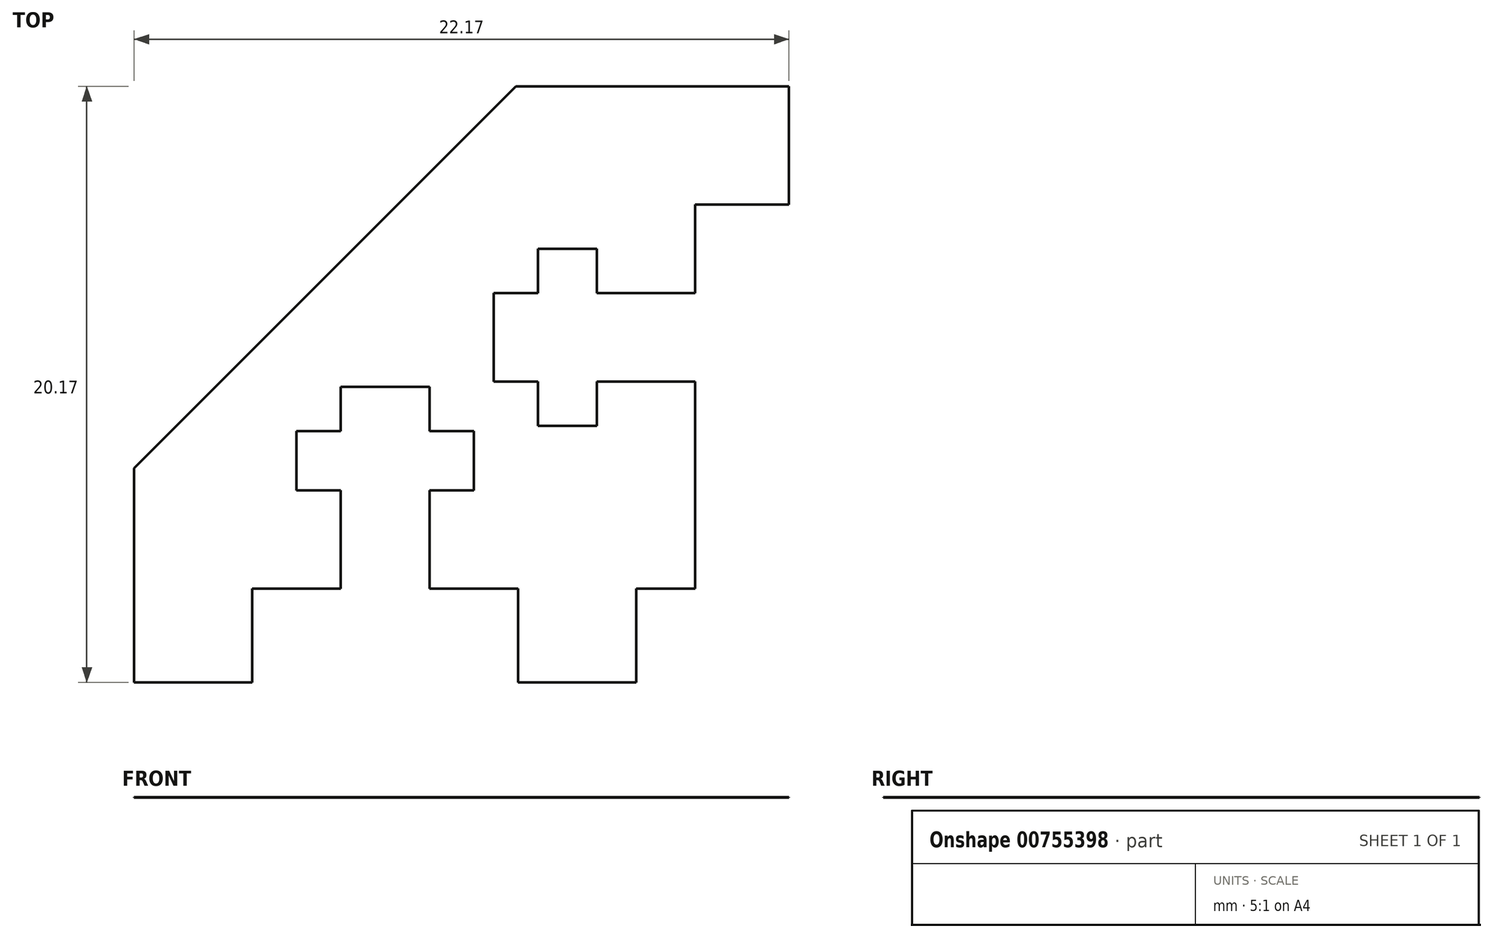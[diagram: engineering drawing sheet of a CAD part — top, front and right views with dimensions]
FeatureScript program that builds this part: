
annotation { "Feature Type Name" : "Feature", "Feature Type Description" : "" }
export const myFeature = defineFeature(function(context is Context, id is Id, definition is map)
    precondition{}
    {
        {
            var Q0;
            Q0=qCreatedBy(makeId("Top.planeOp"),FACE);
            var sketch = newSketch(context, id + "F0", { "sketchPlane" : qUnion([Q0])});
            skLineSegment(sketch, "E0.bottom", {"start": v(-25.65, 8.19) * mm, "end": v(-22.65, 8.19) * mm});
            skLineSegment(sketch, "E0.top", {"start": v(-25.65, -1.81) * mm, "end": v(-22.65, -1.81) * mm});
            skLineSegment(sketch, "E0.left", {"start": v(-25.65, 8.19) * mm, "end": v(-25.65, -1.81) * mm});
            skLineSegment(sketch, "E0.right", {"start": v(-22.65, 8.19) * mm, "end": v(-22.65, -1.81) * mm});
            skPoint(sketch, "E0.middle", {"position": v(-24.15, 3.19) * mm});
            skLineSegment(sketch, "E1.bottom", {"start": v(-27.15, 4.69) * mm, "end": v(-21.15, 4.69) * mm});
            skLineSegment(sketch, "E1.top", {"start": v(-27.15, 6.69) * mm, "end": v(-21.15, 6.69) * mm});
            skLineSegment(sketch, "E1.left", {"start": v(-27.15, 4.69) * mm, "end": v(-27.15, 6.69) * mm});
            skLineSegment(sketch, "E1.right", {"start": v(-21.15, 4.69) * mm, "end": v(-21.15, 6.69) * mm});
            skPoint(sketch, "E1.middle", {"position": v(-24.15, 5.69) * mm});
            skLineSegment(sketch, "E2", {"start": v(-24.15, 5.69) * mm, "end": v(-24.15, 3.19) * mm});
            skLineSegment(sketch, "E3.bottom", {"start": v(-28.65, -1.81) * mm, "end": v(-32.65, -1.81) * mm});
            skLineSegment(sketch, "E3.top", {"start": v(-28.65, 1.36) * mm, "end": v(-32.65, 1.36) * mm});
            skLineSegment(sketch, "E3.left", {"start": v(-28.65, -1.81) * mm, "end": v(-28.65, 1.36) * mm});
            skLineSegment(sketch, "E3.right", {"start": v(-32.65, -1.81) * mm, "end": v(-32.65, 1.36) * mm});
            skLineSegment(sketch, "E4.MirrorCS", {"start": v(-19.65, 1.36) * mm, "end": v(-15.65, 1.36) * mm});
            skLineSegment(sketch, "E5.MirrorCS", {"start": v(-19.65, -1.81) * mm, "end": v(-19.65, 1.36) * mm});
            skLineSegment(sketch, "E6.MirrorCS", {"start": v(-15.65, -1.81) * mm, "end": v(-15.65, 1.36) * mm});
            skLineSegment(sketch, "E7.MirrorCS", {"start": v(-19.65, -1.81) * mm, "end": v(-15.65, -1.81) * mm});
            skLineSegment(sketch, "E8", {"start": v(-19.65, 1.36) * mm, "end": v(-28.65, 1.36) * mm});
            skLineSegment(sketch, "E9.bottom", {"start": v(-28.65, 1.36) * mm, "end": v(-15.65, 1.36) * mm});
            skLineSegment(sketch, "E10.bottom", {"start": v(-20.48, 11.36) * mm, "end": v(-10.48, 11.36) * mm});
            skLineSegment(sketch, "E10.top", {"start": v(-20.48, 8.36) * mm, "end": v(-10.48, 8.36) * mm});
            skLineSegment(sketch, "E10.left", {"start": v(-20.48, 11.36) * mm, "end": v(-20.48, 8.36) * mm});
            skLineSegment(sketch, "E10.right", {"start": v(-10.48, 11.36) * mm, "end": v(-10.48, 8.36) * mm});
            skPoint(sketch, "E10.middle", {"position": v(-15.48, 9.86) * mm});
            skLineSegment(sketch, "E11.bottom", {"start": v(-18.98, 12.86) * mm, "end": v(-16.98, 12.86) * mm});
            skLineSegment(sketch, "E11.top", {"start": v(-18.98, 6.86) * mm, "end": v(-16.98, 6.86) * mm});
            skLineSegment(sketch, "E11.left", {"start": v(-18.98, 12.86) * mm, "end": v(-18.98, 6.86) * mm});
            skLineSegment(sketch, "E11.right", {"start": v(-16.98, 12.86) * mm, "end": v(-16.98, 6.86) * mm});
            skPoint(sketch, "E11.middle", {"position": v(-17.98, 9.86) * mm});
            skLineSegment(sketch, "E12", {"start": v(-17.98, 9.86) * mm, "end": v(-15.48, 9.86) * mm});
            skLineSegment(sketch, "E13.bottom", {"start": v(-10.48, 5.36) * mm, "end": v(-13.65, 5.36) * mm});
            skLineSegment(sketch, "E13.top", {"start": v(-10.48, 1.36) * mm, "end": v(-13.65, 1.36) * mm});
            skLineSegment(sketch, "E13.left", {"start": v(-10.48, 5.36) * mm, "end": v(-10.48, 1.36) * mm});
            skLineSegment(sketch, "E13.right", {"start": v(-13.65, 5.36) * mm, "end": v(-13.65, 1.36) * mm});
            skLineSegment(sketch, "E14.MirrorCS", {"start": v(-10.48, 14.36) * mm, "end": v(-13.65, 14.36) * mm});
            skLineSegment(sketch, "E15.MirrorCS", {"start": v(-13.65, 14.36) * mm, "end": v(-13.65, 18.36) * mm});
            skLineSegment(sketch, "E16.MirrorCS", {"start": v(-10.48, 14.36) * mm, "end": v(-10.48, 18.36) * mm});
            skLineSegment(sketch, "E17.MirrorCS", {"start": v(-10.48, 18.36) * mm, "end": v(-13.65, 18.36) * mm});
            skLineSegment(sketch, "E18.bottom", {"start": v(-13.65, 18.36) * mm, "end": v(-32.65, 18.36) * mm});
            skLineSegment(sketch, "E18.top", {"start": v(-13.65, 1.36) * mm, "end": v(-32.65, 1.36) * mm});
            skLineSegment(sketch, "E18.left", {"start": v(-13.65, 18.36) * mm, "end": v(-13.65, 1.36) * mm});
            skLineSegment(sketch, "E18.right", {"start": v(-32.65, 18.36) * mm, "end": v(-32.65, 1.36) * mm});
            skLineSegment(sketch, "E19", {"start": v(-19.72, 18.36) * mm, "end": v(-32.65, 5.43) * mm});
            skSolve(sketch);
        }
        {
            var Q0;
            Q0=makeQuery(id+"F0.imprint","IMPRINT",FACE,{"disambiguationData":[TD([[makeQuery(id+"F0.imprint","IMPRINT",EDGE,{"derivedFrom":sQuery(id+"F0.wireOp",EDGE,"E3.top")}),-1.0]])]});
            var Q1;
            Q1=makeQuery(id+"F0.imprint","IMPRINT",FACE,{"disambiguationData":[TD([[makeQuery(id+"F0.imprint","IMPRINT",EDGE,{"derivedFrom":sQuery(id+"F0.wireOp",EDGE,"E3.bottom")}),-1.0]])]});
            var Q2;
            {var subQ13=sQuery(id+"F0.wireOp",EDGE,"E0.bottom");Q2=makeQuery(id+"F0.imprint","IMPRINT",FACE,{"disambiguationData":[TD([[makeQuery(id+"F0.imprint","IMPRINT",EDGE,{"derivedFrom":subQ13}),1.0]])]});}
            var Q3;
            {var subQ0=sQuery(id+"F0.wireOp",EDGE,"E5.MirrorCS");Q3=makeQuery(id+"F0.imprint","IMPRINT",FACE,{"disambiguationData":[TD([[makeQuery(id+"F0.imprint","IMPRINT",EDGE,{"derivedFrom":subQ0}),-1.0]])]});}
            var Q4;
            {var subQ0=sQuery(id+"F0.wireOp",EDGE,"E14.MirrorCS");Q4=makeQuery(id+"F0.imprint","IMPRINT",FACE,{"disambiguationData":[TD([[makeQuery(id+"F0.imprint","IMPRINT",EDGE,{"derivedFrom":subQ0}),-1.0]])]});}
            extrude(context, id + "F1", {"entities" : qUnion([Q0, Q1, Q2, Q3, Q4]), "depth" : 1 / 203.2 * mm, "offsetDistance" : 25 * mm});
        }
    });
